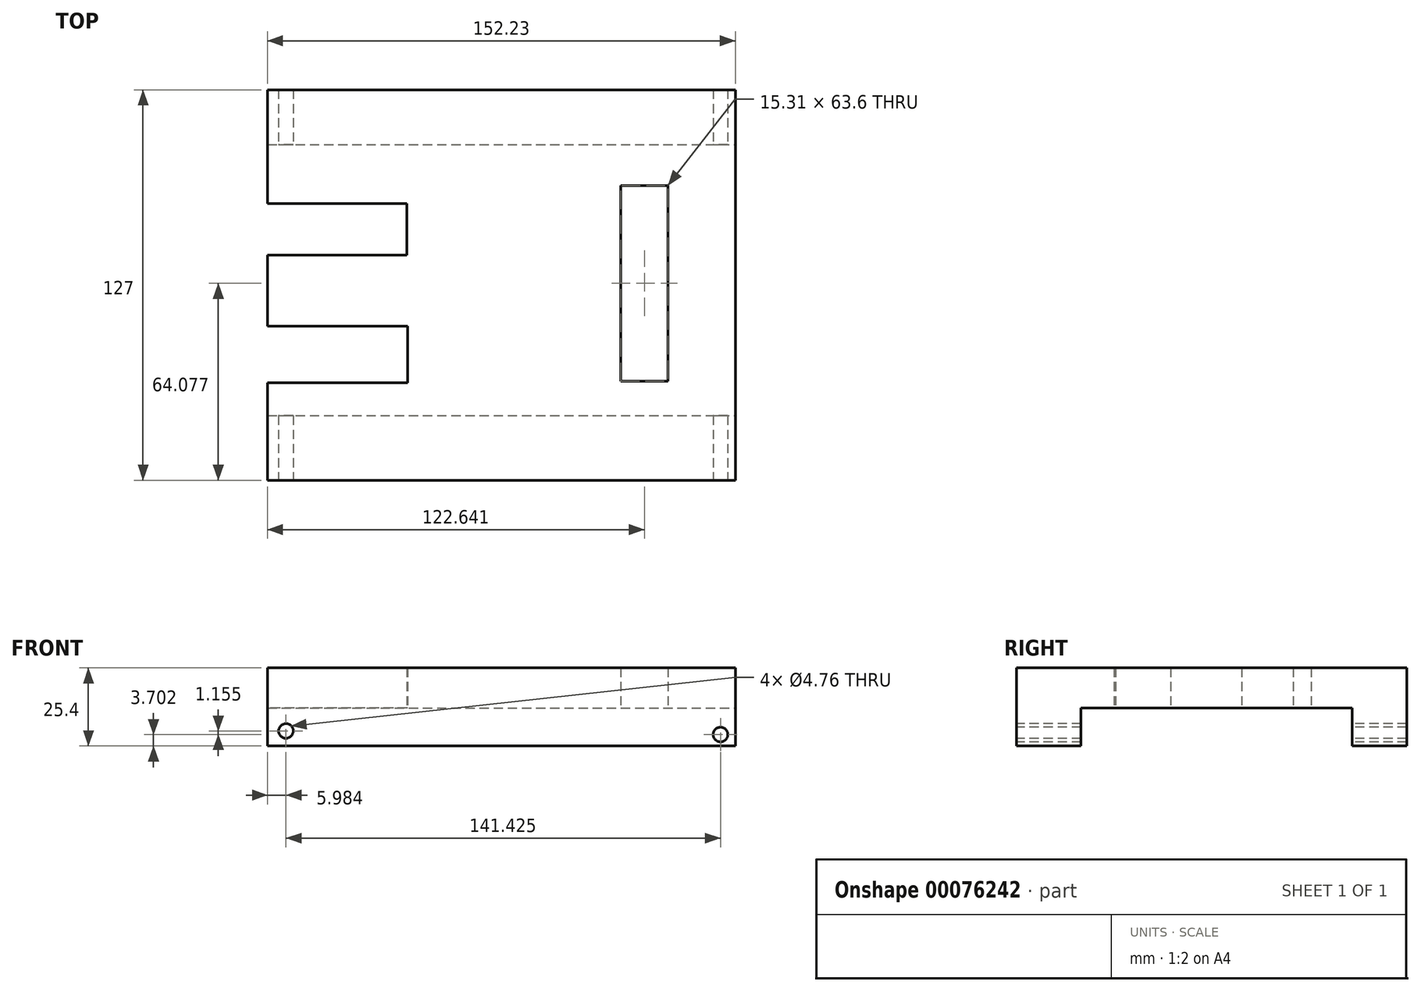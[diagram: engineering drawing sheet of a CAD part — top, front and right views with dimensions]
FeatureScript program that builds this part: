
annotation { "Feature Type Name" : "Feature", "Feature Type Description" : "" }
export const myFeature = defineFeature(function(context is Context, id is Id, definition is map)
    precondition{}
    {
        {
            var Q0;
            Q0=qCreatedBy(makeId("Right.planeOp"),FACE);
            var sketch = newSketch(context, id + "F0", { "sketchPlane" : qUnion([Q0])});
            skLineSegment(sketch, "E0.bottom", {"start": v(-127, 25.4) * mm, "end": v(0, 25.4) * mm});
            skLineSegment(sketch, "E0.top", {"start": v(-127, 0) * mm, "end": v(0, 0) * mm});
            skLineSegment(sketch, "E0.left", {"start": v(-127, 25.4) * mm, "end": v(-127, 0) * mm});
            skLineSegment(sketch, "E0.right", {"start": v(0, 25.4) * mm, "end": v(0, 0) * mm});
            skSolve(sketch);
        }
        {
            var Q0;
            Q0=makeQuery(id+"F0.imprint","IMPRINT",FACE,{"disambiguationData":[TD([[makeQuery(id+"F0.imprint","IMPRINT",EDGE,{"derivedFrom":sQuery(id+"F0.wireOp",EDGE,"E0.bottom")}),-1.0]])]});
            extrude(context, id + "F1", {"entities" : qUnion([Q0]), "depth" : 25.4 * mm});
        }
        {
            var Q0;
            Q0=makeQuery(id+"F1.opExtrude","CAP_FACE",FACE,{"disambiguationData":[OSD([sQuery(id+"F0.wireOp",EDGE,"E0.bottom"),sQuery(id+"F0.wireOp",EDGE,"E0.top"),sQuery(id+"F0.wireOp",EDGE,"E0.left"),sQuery(id+"F0.wireOp",EDGE,"E0.right")])],"isStart":false});
            extrude(context, id + "F2", {"entities" : qUnion([Q0]), "operationType" : NewBodyOperationType.ADD, "depth" : 126.83 * mm});
        }
        {
            var Q0;
            Q0=makeQuery(id+"F2.opExtrude","CAP_FACE",FACE,{"disambiguationData":[OSD([sQuery(id+"F0.wireOp",EDGE,"E0.bottom"),sQuery(id+"F0.wireOp",EDGE,"E0.top"),sQuery(id+"F0.wireOp",EDGE,"E0.left"),sQuery(id+"F0.wireOp",EDGE,"E0.right")])],"isStart":false});
            var sketch = newSketch(context, id + "F3", { "sketchPlane" : qUnion([Q0])});
            skLineSegment(sketch, "E1.bottom", {"start": v(-105.99, 12.38) * mm, "end": v(-17.76, 12.38) * mm});
            skLineSegment(sketch, "E1.top", {"start": v(-105.99, 0) * mm, "end": v(-17.76, 0) * mm});
            skLineSegment(sketch, "E1.left", {"start": v(-105.99, 12.38) * mm, "end": v(-105.99, 0) * mm});
            skLineSegment(sketch, "E1.right", {"start": v(-17.76, 12.38) * mm, "end": v(-17.76, 0) * mm});
            skSolve(sketch);
        }
        {
            var Q0;
            Q0=makeQuery(id+"F3.imprint","IMPRINT",FACE,{"disambiguationData":[TD([[makeQuery(id+"F3.imprint","IMPRINT",EDGE,{"derivedFrom":sQuery(id+"F3.wireOp",EDGE,"E1.bottom")}),-1.0]])]});
            var Q1;
            Q1=sQuery(id+"F3.wireOp",EDGE,"E1.bottom");
            var Q2;
            Q2=sQuery(id+"F3.wireOp",EDGE,"E1.left");
            var Q3;
            Q3=sQuery(id+"F3.wireOp",EDGE,"E1.top");
            var Q4;
            Q4=sQuery(id+"F3.wireOp",EDGE,"E1.right");
            extrude(context, id + "F4", {"entities" : qUnion([Q0]), "operationType" : NewBodyOperationType.REMOVE, "surfaceEntities" : qUnion([Q1, Q2, Q3, Q4]), "endBound" : BoundingType.THROUGH_ALL, "oppositeDirection" : true, "depth" : 25.4 * mm});
        }
        {
            var Q0;
            {var subQ0=sQuery(id+"F0.wireOp",EDGE,"E0.left");Q0=makeQuery(id+"F2.boolean.opBoolean","MERGE",FACE,{"derivedFrom":[makeQuery(id+"F1.opExtrude","SWEPT_FACE",FACE,{"disambiguationData":[OSD([subQ0])]}),makeQuery(id+"F2.opExtrude","SWEPT_FACE",FACE,{"disambiguationData":[OSD([subQ0])]})]});}
            var sketch = newSketch(context, id + "F5", { "sketchPlane" : qUnion([Q0])});
            skCircle(sketch, "E2", {"center": v(147.4, 3.7) * mm, "radius": 2.38 * mm});
            skSolve(sketch);
        }
        {
            var Q0;
            Q0=makeQuery(id+"F5.imprint","IMPRINT",FACE,{"disambiguationData":[TD([[makeQuery(id+"F5.imprint","IMPRINT",EDGE,{"derivedFrom":sQuery(id+"F5.wireOp",EDGE,"E2")}),1.0]])]});
            extrude(context, id + "F6", {"entities" : qUnion([Q0]), "operationType" : NewBodyOperationType.REMOVE, "endBound" : BoundingType.THROUGH_ALL, "oppositeDirection" : true, "depth" : 25.4 * mm});
        }
        {
            var Q0;
            {var subQ0=sQuery(id+"F0.wireOp",EDGE,"E0.left");Q0=makeQuery(id+"F2.boolean.opBoolean","MERGE",FACE,{"derivedFrom":[makeQuery(id+"F1.opExtrude","SWEPT_FACE",FACE,{"disambiguationData":[OSD([subQ0])]}),makeQuery(id+"F2.opExtrude","SWEPT_FACE",FACE,{"disambiguationData":[OSD([subQ0])]})]});}
            var sketch = newSketch(context, id + "F7", { "sketchPlane" : qUnion([Q0])});
            skCircle(sketch, "E3", {"center": v(5.98, 4.86) * mm, "radius": 2.38 * mm});
            skSolve(sketch);
        }
        {
            var Q0;
            Q0=makeQuery(id+"F7.imprint","IMPRINT",FACE,{"disambiguationData":[TD([[makeQuery(id+"F7.imprint","IMPRINT",EDGE,{"derivedFrom":sQuery(id+"F7.wireOp",EDGE,"E3")}),1.0]])]});
            var Q1;
            Q1=sQuery(id+"F7.wireOp",EDGE,"E3");
            extrude(context, id + "F8", {"entities" : qUnion([Q0]), "operationType" : NewBodyOperationType.REMOVE, "surfaceEntities" : qUnion([Q1]), "endBound" : BoundingType.THROUGH_ALL, "oppositeDirection" : true, "depth" : 25.4 * mm});
        }
        {
            var Q0;
            Q0=makeQuery(id+"F4.boolean.opBoolean","COPY",FACE,{"derivedFrom":makeQuery(id+"F4.opExtrude","SWEPT_FACE",FACE,{"disambiguationData":[OSD([sQuery(id+"F3.wireOp",EDGE,"E1.bottom")])]})});
            var sketch = newSketch(context, id + "F9", { "sketchPlane" : qUnion([Q0])});
            skLineSegment(sketch, "E4.bottom", {"start": v(45.33, 37) * mm, "end": v(0, 37) * mm});
            skLineSegment(sketch, "E4.top", {"start": v(45.33, 53.71) * mm, "end": v(0, 53.71) * mm});
            skLineSegment(sketch, "E4.left", {"start": v(45.33, 37) * mm, "end": v(45.33, 53.71) * mm});
            skLineSegment(sketch, "E4.right", {"start": v(0, 37) * mm, "end": v(0, 53.71) * mm});
            skLineSegment(sketch, "E5.bottom", {"start": v(45.56, 95.3) * mm, "end": v(0, 95.3) * mm});
            skLineSegment(sketch, "E5.top", {"start": v(45.56, 76.8) * mm, "end": v(0, 76.8) * mm});
            skLineSegment(sketch, "E5.left", {"start": v(45.56, 95.3) * mm, "end": v(45.56, 76.8) * mm});
            skLineSegment(sketch, "E5.right", {"start": v(0, 95.3) * mm, "end": v(0, 76.8) * mm});
            skLineSegment(sketch, "E6.bottom", {"start": v(114.98, 31.12) * mm, "end": v(130.3, 31.12) * mm});
            skLineSegment(sketch, "E6.top", {"start": v(114.98, 94.73) * mm, "end": v(130.3, 94.73) * mm});
            skLineSegment(sketch, "E6.left", {"start": v(114.98, 31.12) * mm, "end": v(114.98, 94.73) * mm});
            skLineSegment(sketch, "E6.right", {"start": v(130.3, 31.12) * mm, "end": v(130.3, 94.73) * mm});
            skSolve(sketch);
        }
        {
            var Q0;
            Q0=makeQuery(id+"F9.imprint","IMPRINT",FACE,{"disambiguationData":[TD([[makeQuery(id+"F9.imprint","IMPRINT",EDGE,{"derivedFrom":sQuery(id+"F9.wireOp",EDGE,"E5.bottom")}),1.0]])]});
            var Q1;
            Q1=makeQuery(id+"F9.imprint","IMPRINT",FACE,{"disambiguationData":[TD([[makeQuery(id+"F9.imprint","IMPRINT",EDGE,{"derivedFrom":sQuery(id+"F9.wireOp",EDGE,"E4.bottom")}),-1.0]])]});
            var Q2;
            Q2=makeQuery(id+"F9.imprint","IMPRINT",FACE,{"disambiguationData":[TD([[makeQuery(id+"F9.imprint","IMPRINT",EDGE,{"derivedFrom":sQuery(id+"F9.wireOp",EDGE,"E6.bottom")}),1.0]])]});
            extrude(context, id + "F10", {"entities" : qUnion([Q0, Q1, Q2]), "operationType" : NewBodyOperationType.REMOVE, "endBound" : BoundingType.THROUGH_ALL, "oppositeDirection" : true, "depth" : 25.4 * mm});
        }
    });
